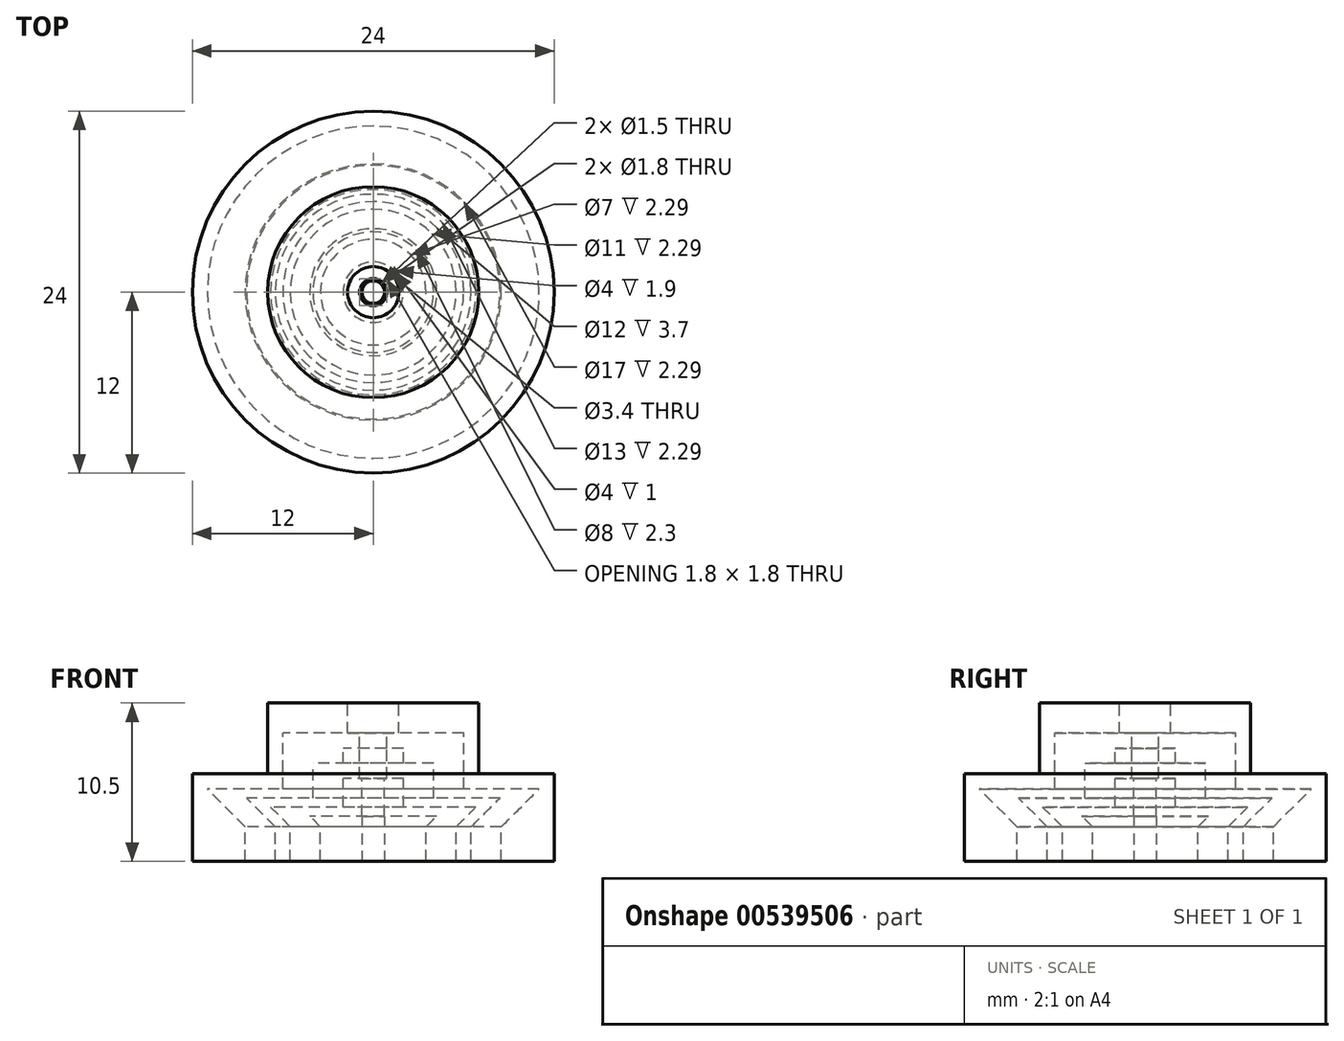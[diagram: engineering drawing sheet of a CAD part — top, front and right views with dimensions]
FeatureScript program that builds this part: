
annotation { "Feature Type Name" : "Feature", "Feature Type Description" : "" }
export const myFeature = defineFeature(function(context is Context, id is Id, definition is map)
    precondition{}
    {
        {
            var Q0;
            Q0=qCreatedBy(makeId("Front.planeOp"),FACE);
            var sketch = newSketch(context, id + "F0", { "sketchPlane" : qUnion([Q0])});
            skLineSegment(sketch, "E0", {"start": v(0, 0) * mm, "end": v(3.5, 0) * mm});
            skLineSegment(sketch, "E1", {"start": v(3.5, 0) * mm, "end": v(3.5, 2.3) * mm});
            skLineSegment(sketch, "E2", {"start": v(3.5, 2.3) * mm, "end": v(4.2, 3) * mm});
            skLineSegment(sketch, "E3", {"start": v(4.2, 3) * mm, "end": v(0, 3) * mm});
            skLineSegment(sketch, "E4", {"start": v(0, 3) * mm, "end": v(0, 0) * mm});
            skLineSegment(sketch, "E5", {"start": v(3.5, 0) * mm, "end": v(5.5, 0) * mm});
            skLineSegment(sketch, "E6", {"start": v(5.5, 0) * mm, "end": v(5.5, 2.3) * mm});
            skLineSegment(sketch, "E7", {"start": v(5.5, 2.3) * mm, "end": v(6.8, 3.6) * mm});
            skLineSegment(sketch, "E8", {"start": v(6.8, 3.6) * mm, "end": v(2, 3.6) * mm});
            skLineSegment(sketch, "E9", {"start": v(2, 3.6) * mm, "end": v(2, 5.5) * mm});
            skLineSegment(sketch, "E10", {"start": v(2, 5.5) * mm, "end": v(0, 5.5) * mm});
            skLineSegment(sketch, "E11", {"start": v(0, 5.5) * mm, "end": v(0, 0) * mm});
            skLineSegment(sketch, "E12", {"start": v(5.5, 0) * mm, "end": v(6.5, 0) * mm});
            skLineSegment(sketch, "E13", {"start": v(6.5, 0) * mm, "end": v(6.5, 2.3) * mm});
            skLineSegment(sketch, "E14", {"start": v(6.5, 2.3) * mm, "end": v(8.4, 4.2) * mm});
            skLineSegment(sketch, "E15", {"start": v(8.4, 4.2) * mm, "end": v(4, 4.2) * mm});
            skLineSegment(sketch, "E16", {"start": v(4, 4.2) * mm, "end": v(4, 6.5) * mm});
            skLineSegment(sketch, "E17", {"start": v(4, 6.5) * mm, "end": v(2, 6.5) * mm});
            skLineSegment(sketch, "E18", {"start": v(2, 6.5) * mm, "end": v(2, 7.5) * mm});
            skLineSegment(sketch, "E19", {"start": v(2, 7.5) * mm, "end": v(0, 7.5) * mm});
            skLineSegment(sketch, "E20", {"start": v(0, 7.5) * mm, "end": v(0, 0) * mm});
            skLineSegment(sketch, "E21", {"start": v(6.5, 0) * mm, "end": v(8.5, 0) * mm});
            skLineSegment(sketch, "E22", {"start": v(8.5, 0) * mm, "end": v(8.5, 2.3) * mm});
            skLineSegment(sketch, "E23", {"start": v(8.5, 2.3) * mm, "end": v(11.01, 4.8) * mm});
            skLineSegment(sketch, "E24", {"start": v(11.01, 4.8) * mm, "end": v(6, 4.8) * mm});
            skLineSegment(sketch, "E25", {"start": v(6, 4.8) * mm, "end": v(6, 8.5) * mm});
            skLineSegment(sketch, "E26", {"start": v(6, 8.5) * mm, "end": v(0, 8.5) * mm});
            skLineSegment(sketch, "E27", {"start": v(0, 8.5) * mm, "end": v(0, 0) * mm});
            skLineSegment(sketch, "E28", {"start": v(8.5, 0) * mm, "end": v(12, 0) * mm});
            skLineSegment(sketch, "E29", {"start": v(12, 0) * mm, "end": v(12, 5.8) * mm});
            skLineSegment(sketch, "E30", {"start": v(12, 5.8) * mm, "end": v(7, 5.8) * mm});
            skLineSegment(sketch, "E31", {"start": v(7, 5.8) * mm, "end": v(7, 10.5) * mm});
            skLineSegment(sketch, "E32", {"start": v(7, 10.5) * mm, "end": v(0, 10.5) * mm});
            skLineSegment(sketch, "E33", {"start": v(0, 10.5) * mm, "end": v(0, 0) * mm});
            skSolve(sketch);
        }
        {
            var Q0;
            Q0=makeQuery(id+"F0.imprint","IMPRINT",FACE,{"disambiguationData":[TD([[makeQuery(id+"F0.imprint","IMPRINT",EDGE,{"derivedFrom":sQuery(id+"F0.wireOp",EDGE,"E0")}),1.0]])]});
            var Q1;
            Q1=sQuery(id+"F0.wireOp",EDGE,"E4");
            revolve(context, id + "F1", {"entities" : qUnion([Q0]), "axis" : qUnion([Q1]), "revolveType" : RevolveType.FULL});
        }
        {
            var Q0;
            Q0=makeQuery(id+"F1.opRevolve","SWEPT_FACE",FACE,{"disambiguationData":[OSD([sQuery(id+"F0.wireOp",EDGE,"E0")])]});
            var sketch = newSketch(context, id + "F2", { "sketchPlane" : qUnion([Q0])});
            skCircle(sketch, "E34", {"center": v(0, 0) * mm, "radius": 0.75 * mm});
            skSolve(sketch);
        }
        {
            var Q0;
            Q0=makeQuery(id+"F2.imprint","IMPRINT",FACE,{"disambiguationData":[TD([[makeQuery(id+"F2.imprint","IMPRINT",EDGE,{"derivedFrom":sQuery(id+"F2.wireOp",EDGE,"E34")}),1.0]])]});
            var Q1;
            Q1=makeQuery(id+"F1.opRevolve","SWEPT_FACE",FACE,{"disambiguationData":[OSD([sQuery(id+"F0.wireOp",EDGE,"E3")])]});
            extrude(context, id + "F3", {"entities" : qUnion([Q0]), "operationType" : NewBodyOperationType.REMOVE, "endBound" : BoundingType.UP_TO_SURFACE, "oppositeDirection" : true, "depth" : 25 * mm, "endBoundEntityFace" : qUnion([Q1]), "offsetDistance" : 25 * mm});
        }
        {
            var Q0;
            Q0=makeQuery(id+"F0.imprint","IMPRINT",FACE,{"disambiguationData":[TD([[makeQuery(id+"F0.imprint","IMPRINT",EDGE,{"derivedFrom":sQuery(id+"F0.wireOp",EDGE,"E1")}),-1.0]])]});
            var Q1;
            Q1=sQuery(id+"F0.wireOp",EDGE,"E11");
            revolve(context, id + "F4", {"entities" : qUnion([Q0]), "axis" : qUnion([Q1]), "revolveType" : RevolveType.FULL});
        }
        {
            var Q0;
            Q0=makeQuery(id+"F4.opRevolve","SWEPT_FACE",FACE,{"disambiguationData":[OSD([sQuery(id+"F0.wireOp",EDGE,"E10")])]});
            var sketch = newSketch(context, id + "F5", { "sketchPlane" : qUnion([Q0])});
            skCircle(sketch, "E35", {"center": v(0, 0) * mm, "radius": 0.75 * mm});
            skSolve(sketch);
        }
        {
            var Q0;
            Q0=makeQuery(id+"F5.imprint","IMPRINT",FACE,{"disambiguationData":[TD([[makeQuery(id+"F5.imprint","IMPRINT",EDGE,{"derivedFrom":sQuery(id+"F5.wireOp",EDGE,"E35")}),1.0]])]});
            extrude(context, id + "F6", {"entities" : qUnion([Q0]), "operationType" : NewBodyOperationType.REMOVE, "endBound" : BoundingType.UP_TO_NEXT, "oppositeDirection" : true, "depth" : 25 * mm, "offsetDistance" : 25 * mm});
        }
        {
            var Q0;
            Q0=makeQuery(id+"F0.imprint","IMPRINT",FACE,{"disambiguationData":[TD([[makeQuery(id+"F0.imprint","IMPRINT",EDGE,{"derivedFrom":sQuery(id+"F0.wireOp",EDGE,"E6")}),-1.0]])]});
            var Q1;
            Q1=sQuery(id+"F0.wireOp",EDGE,"E20");
            revolve(context, id + "F7", {"entities" : qUnion([Q0]), "axis" : qUnion([Q1]), "revolveType" : RevolveType.FULL});
        }
        {
            var Q0;
            Q0=makeQuery(id+"F7.opRevolve","SWEPT_FACE",FACE,{"disambiguationData":[OSD([sQuery(id+"F0.wireOp",EDGE,"E19")])]});
            var sketch = newSketch(context, id + "F8", { "sketchPlane" : qUnion([Q0])});
            skCircle(sketch, "E36", {"center": v(0, 0) * mm, "radius": 0.9 * mm});
            skSolve(sketch);
        }
        {
            var Q0;
            Q0=makeQuery(id+"F8.imprint","IMPRINT",FACE,{"disambiguationData":[TD([[makeQuery(id+"F8.imprint","IMPRINT",EDGE,{"derivedFrom":sQuery(id+"F8.wireOp",EDGE,"E36")}),1.0]])]});
            extrude(context, id + "F9", {"entities" : qUnion([Q0]), "operationType" : NewBodyOperationType.REMOVE, "endBound" : BoundingType.UP_TO_NEXT, "oppositeDirection" : true, "depth" : 25 * mm, "offsetDistance" : 25 * mm});
        }
        {
            var Q0;
            Q0=makeQuery(id+"F0.imprint","IMPRINT",FACE,{"disambiguationData":[TD([[makeQuery(id+"F0.imprint","IMPRINT",EDGE,{"derivedFrom":sQuery(id+"F0.wireOp",EDGE,"E13")}),-1.0]])]});
            var Q1;
            Q1=sQuery(id+"F0.wireOp",EDGE,"E27");
            revolve(context, id + "F10", {"entities" : qUnion([Q0]), "axis" : qUnion([Q1]), "revolveType" : RevolveType.FULL});
        }
        {
            var Q0;
            Q0=makeQuery(id+"F10.opRevolve","SWEPT_FACE",FACE,{"disambiguationData":[OSD([sQuery(id+"F0.wireOp",EDGE,"E26")])]});
            var sketch = newSketch(context, id + "F11", { "sketchPlane" : qUnion([Q0])});
            skCircle(sketch, "E37", {"center": v(0, 0) * mm, "radius": 0.9 * mm});
            skSolve(sketch);
        }
        {
            var Q0;
            Q0=makeQuery(id+"F11.imprint","IMPRINT",FACE,{"disambiguationData":[TD([[makeQuery(id+"F11.imprint","IMPRINT",EDGE,{"derivedFrom":sQuery(id+"F11.wireOp",EDGE,"E37")}),1.0]])]});
            extrude(context, id + "F12", {"entities" : qUnion([Q0]), "operationType" : NewBodyOperationType.REMOVE, "endBound" : BoundingType.UP_TO_NEXT, "oppositeDirection" : true, "depth" : 25 * mm, "offsetDistance" : 25 * mm});
        }
        {
            var Q0;
            Q0=makeQuery(id+"F0.imprint","IMPRINT",FACE,{"disambiguationData":[TD([[makeQuery(id+"F0.imprint","IMPRINT",EDGE,{"derivedFrom":sQuery(id+"F0.wireOp",EDGE,"E22")}),-1.0]])]});
            var Q1;
            Q1=sQuery(id+"F0.wireOp",EDGE,"E33");
            revolve(context, id + "F13", {"entities" : qUnion([Q0]), "axis" : qUnion([Q1]), "revolveType" : RevolveType.FULL});
        }
        {
            var Q0;
            Q0=makeQuery(id+"F13.opRevolve","SWEPT_FACE",FACE,{"disambiguationData":[OSD([sQuery(id+"F0.wireOp",EDGE,"E32")])]});
            var sketch = newSketch(context, id + "F14", { "sketchPlane" : qUnion([Q0])});
            skCircle(sketch, "E38", {"center": v(0, 0) * mm, "radius": 1.7 * mm});
            skSolve(sketch);
        }
        {
            var Q0;
            Q0=makeQuery(id+"F14.imprint","IMPRINT",FACE,{"disambiguationData":[TD([[makeQuery(id+"F14.imprint","IMPRINT",EDGE,{"derivedFrom":sQuery(id+"F14.wireOp",EDGE,"E38")}),1.0]])]});
            extrude(context, id + "F15", {"entities" : qUnion([Q0]), "operationType" : NewBodyOperationType.REMOVE, "endBound" : BoundingType.UP_TO_NEXT, "oppositeDirection" : true, "depth" : 25 * mm, "offsetDistance" : 25 * mm});
        }
    });
